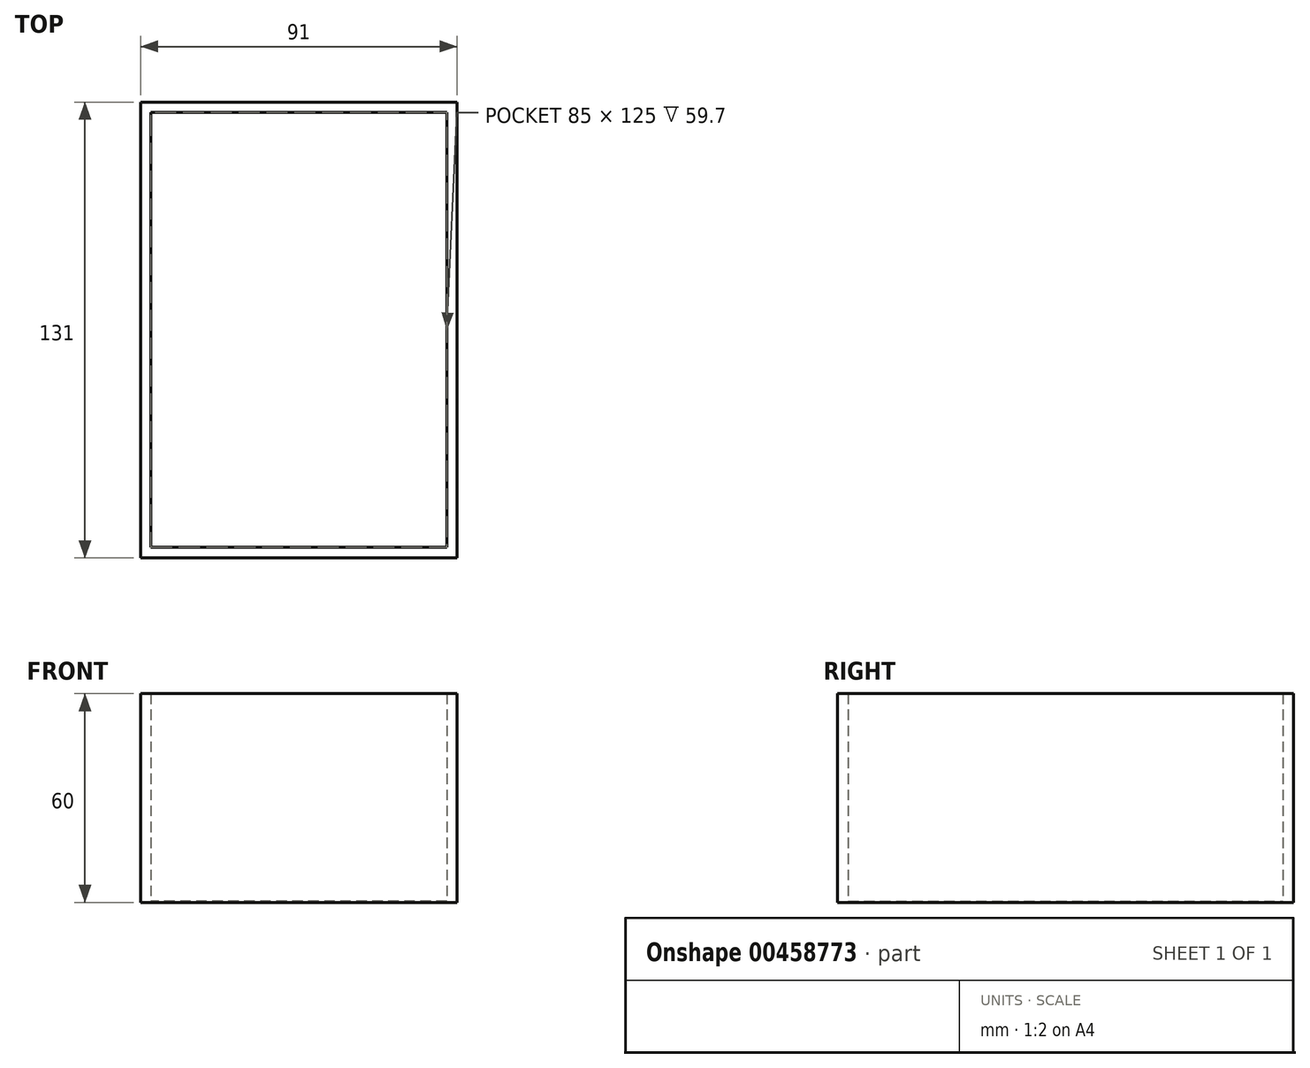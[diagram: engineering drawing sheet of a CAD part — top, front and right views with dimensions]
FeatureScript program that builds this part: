
annotation { "Feature Type Name" : "Feature", "Feature Type Description" : "" }
export const myFeature = defineFeature(function(context is Context, id is Id, definition is map)
    precondition{}
    {
        {
            assignVariable(context, id + "F0", {"name" : "hout", "anyValue" : 0.3});
        }
        {
            var Q0;
            Q0=qCreatedBy(makeId("Top.planeOp"),FACE);
            var sketch = newSketch(context, id + "F1", { "sketchPlane" : qUnion([Q0])});
            skLineSegment(sketch, "E0.bottom", {"start": v(137.5, -137.5) * mm, "end": v(-137.5, -137.5) * mm});
            skLineSegment(sketch, "E0.top", {"start": v(137.5, 137.5) * mm, "end": v(-137.5, 137.5) * mm});
            skLineSegment(sketch, "E0.left", {"start": v(137.5, -137.5) * mm, "end": v(137.5, 137.5) * mm});
            skLineSegment(sketch, "E0.right", {"start": v(-137.5, -137.5) * mm, "end": v(-137.5, 137.5) * mm});
            skPoint(sketch, "E0.middle", {"position": v(0, 0) * mm});
            skLineSegment(sketch, "E1.bottom", {"start": v(-134.5, -9.5) * mm, "end": v(-49.5, -9.5) * mm});
            skLineSegment(sketch, "E1.top", {"start": v(-134.5, -134.5) * mm, "end": v(-49.5, -134.5) * mm});
            skLineSegment(sketch, "E1.left", {"start": v(-134.5, -9.5) * mm, "end": v(-134.5, -134.5) * mm});
            skLineSegment(sketch, "E1.right", {"start": v(-49.5, -9.5) * mm, "end": v(-49.5, -134.5) * mm});
            skLineSegment(sketch, "E2.0", {"start": v(-137.5, -6.5) * mm, "end": v(-46.5, -6.5) * mm});
            skLineSegment(sketch, "E2.1", {"start": v(-137.5, -6.5) * mm, "end": v(-137.5, -137.5) * mm});
            skLineSegment(sketch, "E2.2", {"start": v(-137.5, -137.5) * mm, "end": v(-46.5, -137.5) * mm});
            skLineSegment(sketch, "E2.3", {"start": v(-46.5, -6.5) * mm, "end": v(-46.5, -137.5) * mm});
            skLineSegment(sketch, "E3.bottom", {"start": v(49.5, -9.5) * mm, "end": v(134.5, -9.5) * mm});
            skLineSegment(sketch, "E3.top", {"start": v(49.5, -134.5) * mm, "end": v(134.5, -134.5) * mm});
            skLineSegment(sketch, "E3.left", {"start": v(49.5, -9.5) * mm, "end": v(49.5, -134.5) * mm});
            skLineSegment(sketch, "E3.right", {"start": v(134.5, -9.5) * mm, "end": v(134.5, -134.5) * mm});
            skLineSegment(sketch, "E4.0", {"start": v(46.5, -6.5) * mm, "end": v(137.5, -6.5) * mm});
            skLineSegment(sketch, "E4.1", {"start": v(46.5, -6.5) * mm, "end": v(46.5, -137.5) * mm});
            skLineSegment(sketch, "E4.2", {"start": v(46.5, -137.5) * mm, "end": v(137.5, -137.5) * mm});
            skLineSegment(sketch, "E4.3", {"start": v(137.5, -6.5) * mm, "end": v(137.5, -137.5) * mm});
            skLineSegment(sketch, "E5.bottom", {"start": v(-42.5, -9.5) * mm, "end": v(42.5, -9.5) * mm});
            skLineSegment(sketch, "E5.top", {"start": v(-42.5, -134.5) * mm, "end": v(42.5, -134.5) * mm});
            skLineSegment(sketch, "E5.left", {"start": v(-42.5, -9.5) * mm, "end": v(-42.5, -134.5) * mm});
            skLineSegment(sketch, "E5.right", {"start": v(42.5, -9.5) * mm, "end": v(42.5, -134.5) * mm});
            skLineSegment(sketch, "E6.0", {"start": v(-45.5, -6.5) * mm, "end": v(45.5, -6.5) * mm});
            skLineSegment(sketch, "E6.1", {"start": v(-45.5, -6.5) * mm, "end": v(-45.5, -137.5) * mm});
            skLineSegment(sketch, "E6.2", {"start": v(-45.5, -137.5) * mm, "end": v(45.5, -137.5) * mm});
            skLineSegment(sketch, "E6.3", {"start": v(45.5, -6.5) * mm, "end": v(45.5, -137.5) * mm});
            skPoint(sketch, "E7", {"position": v(0, -137.5) * mm});
            skLineSegment(sketch, "E8.bottom", {"start": v(-134.5, 134.5) * mm, "end": v(-39.5, 134.5) * mm});
            skLineSegment(sketch, "E8.top", {"start": v(-134.5, 31.5) * mm, "end": v(-39.5, 31.5) * mm});
            skLineSegment(sketch, "E8.left", {"start": v(-134.5, 134.5) * mm, "end": v(-134.5, 31.5) * mm});
            skLineSegment(sketch, "E8.right", {"start": v(-39.5, 134.5) * mm, "end": v(-39.5, 31.5) * mm});
            skLineSegment(sketch, "E9.0", {"start": v(-137.5, 137.5) * mm, "end": v(-36.5, 137.5) * mm});
            skLineSegment(sketch, "E9.1", {"start": v(-137.5, 137.5) * mm, "end": v(-137.5, 28.5) * mm});
            skLineSegment(sketch, "E9.2", {"start": v(-137.5, 28.5) * mm, "end": v(-36.5, 28.5) * mm});
            skLineSegment(sketch, "E9.3", {"start": v(-36.5, 137.5) * mm, "end": v(-36.5, 28.5) * mm});
            skSolve(sketch);
        }
        {
            var Q0;
            Q0=makeQuery(id+"F1.imprint","IMPRINT",FACE,{"disambiguationData":[TD([[makeQuery(id+"F1.imprint","IMPRINT",EDGE,{"derivedFrom":sQuery(id+"F1.wireOp",EDGE,"E3.bottom")}),-1.0]])]});
            var Q1;
            Q1=makeQuery(id+"F1.imprint","IMPRINT",FACE,{"disambiguationData":[TD([[makeQuery(id+"F1.imprint","IMPRINT",EDGE,{"derivedFrom":sQuery(id+"F1.wireOp",EDGE,"E3.bottom")}),1.0]])]});
            extrude(context, id + "F2", {"entities" : qUnion([Q0, Q1]), "depth" : (getVariable(context, 'hout')) * mm});
        }
        {
            var Q0;
            Q0=makeQuery(id+"F1.imprint","IMPRINT",FACE,{"disambiguationData":[TD([[makeQuery(id+"F1.imprint","IMPRINT",EDGE,{"derivedFrom":sQuery(id+"F1.wireOp",EDGE,"E3.bottom")}),1.0]])]});
            extrude(context, id + "F3", {"entities" : qUnion([Q0]), "operationType" : NewBodyOperationType.ADD, "depth" : 60 * mm});
        }
    });
